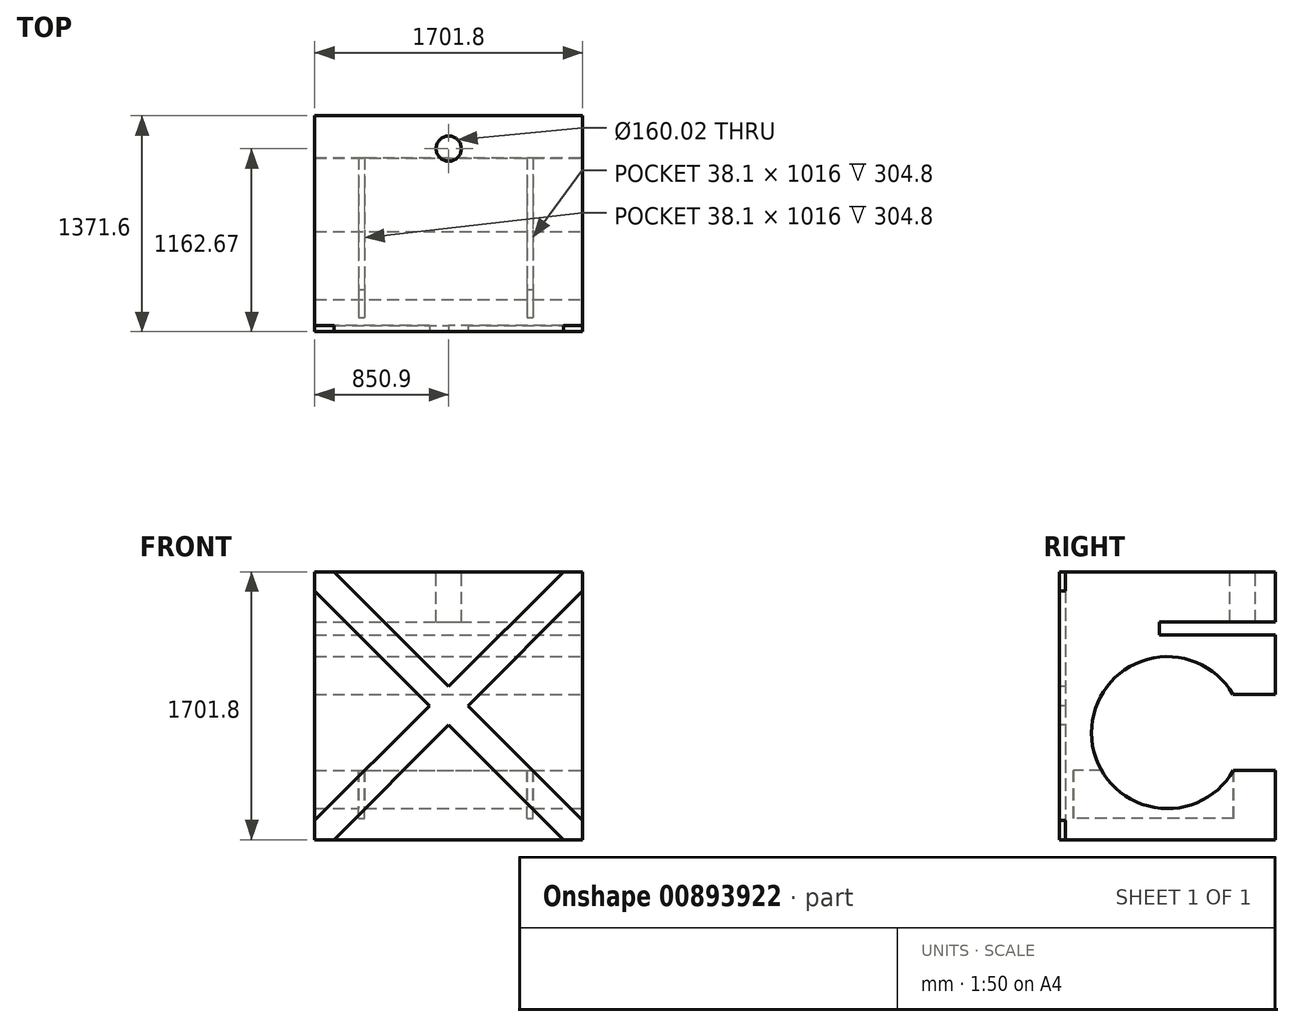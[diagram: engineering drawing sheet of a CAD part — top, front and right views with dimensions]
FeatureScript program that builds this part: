
annotation { "Feature Type Name" : "Feature", "Feature Type Description" : "" }
export const myFeature = defineFeature(function(context is Context, id is Id, definition is map)
    precondition{}
    {
        {
            var Q0;
            Q0=qCreatedBy(makeId("Front.planeOp"),FACE);
            var sketch = newSketch(context, id + "F0", { "sketchPlane" : qUnion([Q0])});
            skLineSegment(sketch, "E0.bottom", {"start": v(850.9, -850.9) * mm, "end": v(-850.9, -850.9) * mm});
            skLineSegment(sketch, "E0.top", {"start": v(850.9, 850.9) * mm, "end": v(-850.9, 850.9) * mm});
            skLineSegment(sketch, "E0.left", {"start": v(850.9, -850.9) * mm, "end": v(850.9, 850.9) * mm});
            skLineSegment(sketch, "E0.right", {"start": v(-850.9, -850.9) * mm, "end": v(-850.9, 850.9) * mm});
            skPoint(sketch, "E0.middle", {"position": v(0, 0) * mm});
            skSolve(sketch);
        }
        {
            var Q0;
            Q0=qSketchRegion(id+"F0",true);
            extrude(context, id + "F1", {"entities" : qUnion([Q0]), "depth" : 685.8 * mm, "hasSecondDirection" : true, "secondDirectionOppositeDirection" : true, "secondDirectionDepth" : 685.8 * mm});
        }
        {
            var Q0;
            Q0=makeQuery(id+"F1.opExtrude","SWEPT_FACE",FACE,{"disambiguationData":[OSD([sQuery(id+"F0.wireOp",EDGE,"E0.left")])]});
            var sketch = newSketch(context, id + "F2", { "sketchPlane" : qUnion([Q0])});
            skLineSegment(sketch, "E1", {"start": v(0, -850.9) * mm, "end": v(0, -165.1) * mm});
            skSolve(sketch);
        }
        {
            var Q0;
            {var subQ0=sQuery(id+"F0.wireOp",EDGE,"E0.left");var subQ1=makeQuery(id+"F1.opExtrude","CAP_EDGE",EDGE,{"disambiguationData":[OSD([subQ0])],"isStart":true});Q0=makeQuery(id+"F2.imprint","IMPRINT",FACE,{"disambiguationData":[TD([[makeQuery(id+"F2.imprint","IMPRINT",EDGE,{"derivedFrom":subQ1}),1.0]])]});}
            var sketch = newSketch(context, id + "F3", { "sketchPlane" : qUnion([Q0])});
            skCircle(sketch, "E2", {"center": v(0, -170.7) * mm, "radius": 482.6 * mm});
            skSolve(sketch);
        }
        {
            var Q0;
            {var subQ0=sQuery(id+"F0.wireOp",EDGE,"E0.left");var subQ1=makeQuery(id+"F1.opExtrude","CAP_EDGE",EDGE,{"disambiguationData":[OSD([subQ0])],"isStart":true});Q0=makeQuery(id+"F2.imprint","IMPRINT",FACE,{"disambiguationData":[TD([[makeQuery(id+"F2.imprint","IMPRINT",EDGE,{"derivedFrom":subQ1}),1.0]])]});}
            var sketch = newSketch(context, id + "F4", { "sketchPlane" : qUnion([Q0])});
            skLineSegment(sketch, "E3.bottom", {"start": v(0, -168.4) * mm, "end": v(741.85, -168.4) * mm});
            skLineSegment(sketch, "E3.top", {"start": v(0, -409.7) * mm, "end": v(741.85, -409.7) * mm});
            skLineSegment(sketch, "E3.left", {"start": v(0, -168.4) * mm, "end": v(0, -409.7) * mm});
            skLineSegment(sketch, "E3.right", {"start": v(741.85, -168.4) * mm, "end": v(741.85, -409.7) * mm});
            skLineSegment(sketch, "E4.bottom", {"start": v(0, -168.4) * mm, "end": v(741.2, -168.4) * mm});
            skLineSegment(sketch, "E4.top", {"start": v(0, 72.9) * mm, "end": v(741.2, 72.9) * mm});
            skLineSegment(sketch, "E4.left", {"start": v(0, -168.4) * mm, "end": v(0, 72.9) * mm});
            skLineSegment(sketch, "E4.right", {"start": v(741.2, -168.4) * mm, "end": v(741.2, 72.9) * mm});
            skSolve(sketch);
        }
        {
            var Q0;
            Q0=qSketchRegion(id+"F3",true);
            extrude(context, id + "F5", {"entities" : qUnion([Q0]), "operationType" : NewBodyOperationType.REMOVE, "oppositeDirection" : true, "depth" : 1778 * mm});
        }
        {
            var Q0;
            Q0=qSketchRegion(id+"F4",true);
            extrude(context, id + "F6", {"entities" : qUnion([Q0]), "operationType" : NewBodyOperationType.REMOVE, "oppositeDirection" : true, "depth" : 1778 * mm});
        }
        {
            var Q0;
            {var subQ0=sQuery(id+"F0.wireOp",EDGE,"E0.left");var subQ1=makeQuery(id+"F1.opExtrude","CAP_EDGE",EDGE,{"disambiguationData":[OSD([subQ0])],"isStart":true});Q0=makeQuery(id+"F2.imprint","IMPRINT",FACE,{"disambiguationData":[TD([[makeQuery(id+"F2.imprint","IMPRINT",EDGE,{"derivedFrom":subQ1}),1.0]])]});}
            var sketch = newSketch(context, id + "F7", { "sketchPlane" : qUnion([Q0])});
            skLineSegment(sketch, "E5.bottom", {"start": v(-50, 532.54) * mm, "end": v(712, 532.54) * mm});
            skLineSegment(sketch, "E5.top", {"start": v(-50, 448.72) * mm, "end": v(712, 448.72) * mm});
            skLineSegment(sketch, "E5.left", {"start": v(-50, 532.54) * mm, "end": v(-50, 448.72) * mm});
            skLineSegment(sketch, "E5.right", {"start": v(712, 532.54) * mm, "end": v(712, 448.72) * mm});
            skSolve(sketch);
        }
        {
            var Q0;
            Q0=qSketchRegion(id+"F7",true);
            extrude(context, id + "F8", {"entities" : qUnion([Q0]), "operationType" : NewBodyOperationType.REMOVE, "oppositeDirection" : true, "depth" : 1778 * mm});
        }
        {
            var Q0;
            Q0=makeQuery(id+"F1.opExtrude","CAP_FACE",FACE,{"disambiguationData":[OSD([sQuery(id+"F0.wireOp",EDGE,"E0.bottom"),sQuery(id+"F0.wireOp",EDGE,"E0.top"),sQuery(id+"F0.wireOp",EDGE,"E0.left"),sQuery(id+"F0.wireOp",EDGE,"E0.right")])],"isStart":false});
            var sketch = newSketch(context, id + "F9", { "sketchPlane" : qUnion([Q0])});
            skLineSegment(sketch, "E6", {"start": v(850.9, 850.9) * mm, "end": v(850.9, 728.98) * mm});
            skLineSegment(sketch, "E7", {"start": v(850.9, 850.9) * mm, "end": v(728.98, 850.9) * mm});
            skLineSegment(sketch, "E8", {"start": v(-850.9, -850.9) * mm, "end": v(-728.98, -850.9) * mm});
            skLineSegment(sketch, "E9", {"start": v(-850.9, -850.9) * mm, "end": v(-850.9, -728.98) * mm});
            skLineSegment(sketch, "E10", {"start": v(728.98, 850.9) * mm, "end": v(-850.9, -728.98) * mm});
            skLineSegment(sketch, "E11", {"start": v(850.9, 728.98) * mm, "end": v(-728.98, -850.9) * mm});
            skLineSegment(sketch, "E12", {"start": v(-850.9, 850.9) * mm, "end": v(-850.9, 728.98) * mm});
            skLineSegment(sketch, "E13", {"start": v(-850.9, 850.9) * mm, "end": v(-728.98, 850.9) * mm});
            skLineSegment(sketch, "E14", {"start": v(850.9, -850.9) * mm, "end": v(728.98, -850.9) * mm});
            skLineSegment(sketch, "E15", {"start": v(850.9, -850.9) * mm, "end": v(850.9, -728.98) * mm});
            skLineSegment(sketch, "E16", {"start": v(-728.98, 850.9) * mm, "end": v(850.9, -728.98) * mm});
            skLineSegment(sketch, "E17", {"start": v(-850.9, 728.98) * mm, "end": v(728.98, -850.9) * mm});
            skSolve(sketch);
        }
        {
            var Q0;
            Q0=qSketchRegion(id+"F9",true);
            extrude(context, id + "F10", {"entities" : qUnion([Q0]), "operationType" : NewBodyOperationType.REMOVE, "oppositeDirection" : true, "depth" : 38.1 * mm});
        }
        {
            var Q0;
            Q0=makeQuery(id+"F1.opExtrude","SWEPT_FACE",FACE,{"disambiguationData":[OSD([sQuery(id+"F0.wireOp",EDGE,"E0.top")])]});
            var sketch = newSketch(context, id + "F11", { "sketchPlane" : qUnion([Q0])});
            skLineSegment(sketch, "E18", {"start": v(-850.9, 685.8) * mm, "end": v(0, 685.8) * mm});
            skLineSegment(sketch, "E19", {"start": v(0, 685.8) * mm, "end": v(0, 474.98) * mm});
            skSolve(sketch);
        }
        {
            var Q0;
            {var subQ4=sQuery(id+"F11.wireOp",EDGE,"E18");Q0=makeQuery(id+"F11.imprint","IMPRINT",FACE,{"disambiguationData":[TD([[makeQuery(id+"F11.imprint","IMPRINT",EDGE,{"derivedFrom":subQ4}),1.0]])]});}
            var sketch = newSketch(context, id + "F12", { "sketchPlane" : qUnion([Q0])});
            skCircle(sketch, "E20", {"center": v(0, 476.87) * mm, "radius": 80.01 * mm});
            skSolve(sketch);
        }
        {
            var Q0;
            Q0=qSketchRegion(id+"F12",true);
            extrude(context, id + "F13", {"entities" : qUnion([Q0]), "operationType" : NewBodyOperationType.REMOVE, "oppositeDirection" : true, "depth" : 320.04 * mm});
        }
        {
            var Q0;
            Q0=makeQuery(id+"F6.boolean.opBoolean","COPY",FACE,{"derivedFrom":makeQuery(id+"F6.opExtrude","SWEPT_FACE",FACE,{"disambiguationData":[OSD([sQuery(id+"F4.wireOp",EDGE,"E3.top")])]})});
            var sketch = newSketch(context, id + "F14", { "sketchPlane" : qUnion([Q0])});
            skLineSegment(sketch, "E21", {"start": v(850.9, 685.8) * mm, "end": v(533.4, 685.8) * mm});
            skLineSegment(sketch, "E22", {"start": v(533.4, 685.8) * mm, "end": v(533.4, 419.27) * mm});
            skLineSegment(sketch, "E23", {"start": v(533.4, 419.27) * mm, "end": v(-533.4, 419.27) * mm});
            skSolve(sketch);
        }
        {
            var Q0;
            Q0=makeQuery(id+"F14.imprint","IMPRINT",FACE,{"disambiguationData":[TD([[makeQuery(id+"F14.imprint","IMPRINT",EDGE,{"derivedFrom":sQuery(id+"F14.wireOp",EDGE,"E21")}),-1.0]])]});
            var sketch = newSketch(context, id + "F15", { "sketchPlane" : qUnion([Q0])});
            skLineSegment(sketch, "E24.bottom", {"start": v(495.6, 420.67) * mm, "end": v(533.7, 420.67) * mm});
            skLineSegment(sketch, "E24.top", {"start": v(495.6, -595.33) * mm, "end": v(533.7, -595.33) * mm});
            skLineSegment(sketch, "E24.left", {"start": v(495.6, 420.67) * mm, "end": v(495.6, -595.33) * mm});
            skLineSegment(sketch, "E24.right", {"start": v(533.7, 420.67) * mm, "end": v(533.7, -595.33) * mm});
            skLineSegment(sketch, "E25.bottom", {"start": v(-571.5, 419.29) * mm, "end": v(-533.4, 419.29) * mm});
            skLineSegment(sketch, "E25.top", {"start": v(-571.5, -596.71) * mm, "end": v(-533.4, -596.71) * mm});
            skLineSegment(sketch, "E25.left", {"start": v(-571.5, 419.29) * mm, "end": v(-571.5, -596.71) * mm});
            skLineSegment(sketch, "E25.right", {"start": v(-533.4, 419.29) * mm, "end": v(-533.4, -596.71) * mm});
            skSolve(sketch);
        }
        {
            var Q0;
            Q0=qSketchRegion(id+"F15",true);
            extrude(context, id + "F16", {"entities" : qUnion([Q0]), "operationType" : NewBodyOperationType.REMOVE, "oppositeDirection" : true, "depth" : 304.8 * mm});
        }
    });
